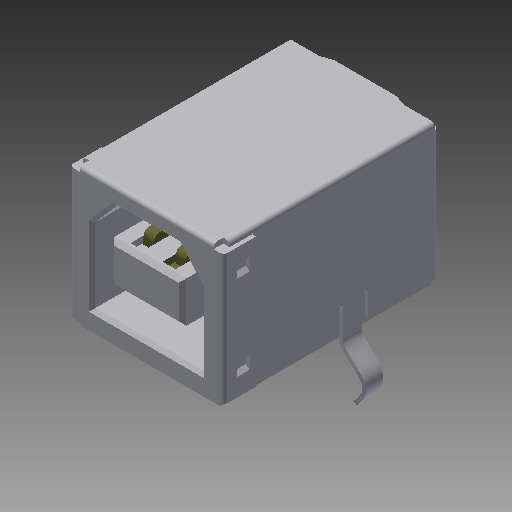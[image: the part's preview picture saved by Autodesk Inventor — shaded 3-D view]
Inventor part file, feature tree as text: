
AUTODESK INVENTOR PART (.ipt)
format: ipt  version: 2018 (Build 220112000, 112)  size: 468,992 bytes
history: native  units: mm
features: mirror x1, imported_body x1
ambient origin geometry x8: Origin, YZ Plane, XZ Plane, XY Plane, X Axis, Y Axis, Z Axis, Center Point
bodies: Body1 (feature_tree)
feature tree (2):
  mirror  "Mirror17"
  imported_body  "Base1"
